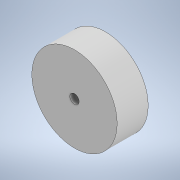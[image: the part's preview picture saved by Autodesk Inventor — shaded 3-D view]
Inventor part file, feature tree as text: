
AUTODESK INVENTOR PART (.ipt)
format: ipt  version: 2020.1 (Build 241239000, 239)  size: 97,280 bytes
history: native  units: mm
features: extrude x1, sketch x1
ambient origin geometry x8: Origin, YZ Plane, XZ Plane, XY Plane, X Axis, Y Axis, Z Axis, Center Point
bodies: Solid1 (feature_tree)
feature tree (2):
  extrude  "Extrusion1"  Depth=40.0mm
  sketch  "Sketch1"  dims[d0=110.0mm d1=12.0mm d2=40.0mm d3=0.0mm]
